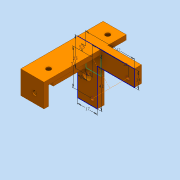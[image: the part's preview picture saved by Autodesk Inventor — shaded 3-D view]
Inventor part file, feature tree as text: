
AUTODESK INVENTOR PART (.ipt)
format: ipt  version: 2016 (Build 200138000, 138)  size: 242,176 bytes
history: native  units: mm
features: extrude x10, sketch x10, hole x7
ambient origin geometry x8: Origin, YZ Plane, XZ Plane, XY Plane, X Axis, Y Axis, Z Axis, Center Point
bodies: Solid1 (feature_tree)
feature tree (27):
  extrude  "Extrusion1"  Depth=20.0mm
  extrude  "Extrusion2"  Depth=45.0mm TaperAngle=0.0deg
  hole  "Hole2"  [1 undecoded]
  hole  "Hole3"  [1 undecoded]
  hole  "Hole4"  [1 undecoded]
  sketch  "Sketch3"  dims[d15=37.0mm d16=8.0mm d17=4.0mm d18=6.0mm d19=8.0mm d20=2.0mm d21=90.0deg d22=8.0mm d23=20.594885mm]
  sketch  "Sketch4"  dims[d24=37.0mm d25=8.0mm d26=4.0mm d27=6.0mm d28=8.0mm d29=2.0mm d30=90.0deg d31=8.0mm d32=20.594885mm]
  sketch  "Sketch5"  dims[d33=8.0mm d34=8.0mm d35=4.0mm d36=6.0mm d37=8.0mm d38=2.0mm d39=90.0deg d40=8.0mm d41=20.594885mm d51=7.0mm]
  extrude  "Extrusion3"  Depth=17.0mm
  extrude  "Extrusion4"  Depth=42.0mm
  extrude  "Extrusion5"  Depth=5.5mm
  sketch  "Sketch6"  dims[d52=7.0mm d53=7.0mm]
  extrude  "Extrusion6"  Depth=10.0mm
  hole  "Hole5"  [1 undecoded]
  extrude  "Extrusion7"  Depth=14.0mm
  hole  "Hole6"  [1 undecoded]
  hole  "Hole7"  [1 undecoded]
  sketch  "Sketch8"  dims[d58=3.2mm d59=0.0mm d62=17.0mm]
  extrude  "Extrusion8"  Depth=4.0mm
  extrude  "Extrusion9"  Depth=4.0mm
  hole  "Hole8"  [1 undecoded]
  extrude  "Extrusion10"  Depth=16.0mm TaperAngle=0.0deg
  sketch  "Sketch1"  dims[d0=20.0mm d1=20.0mm]
  sketch  "Sketch2"  dims[d2=4.0mm d3=0.0mm d4=45.0mm d5=0.0mm]
  sketch  "Sketch7"  dims[d54=3.2mm d55=0.0mm d56=3.2mm d57=0.0mm]
  sketch  "Sketch9"  dims[d65=42.0mm d66=42.0mm]
  sketch  "Sketch11"  dims[d68=5.5mm d69=5.5mm d70=31.0mm d71=31.0mm d72=14.0mm d73=6.0mm d74=0.0mm d75=3.0mm d76=6.0mm d77=4.0mm d78=2.0mm d79=90.0deg d80=8.0mm d81=20.594885mm d82=20.0mm d83=4.0mm d84=4.0mm d85=20.0mm d86=16.0mm d87=0.0mm d88=8.0mm d89=8.0mm d90=4.0mm d91=6.0mm d92=4.0mm d93=2.0mm d94=90.0deg d95=8.0mm d96=20.594885mm d97=8.0mm d98=8.0mm d99=4.0mm d100=6.0mm d101=4.0mm d102=2.0mm d103=90.0deg d104=8.0mm d105=20.594885mm d106=7.0mm d107=7.0mm d108=3.2mm d109=0.0mm d110=3.2mm d111=0.0mm d112=8.0mm d113=25.0mm d114=8.0mm d115=6.0mm d116=4.0mm d117=2.0mm d118=90.0deg d119=8.0mm d120=20.594885mm d121=8.0mm d122=25.0mm d123=7.0mm d127=10.0mm d128=0.0mm]
note: 7 required parameter values undecoded (feature->parameter linkage not recoverable at this tier; creation-order binding heuristic only, values carry confidence <= 0.55)
